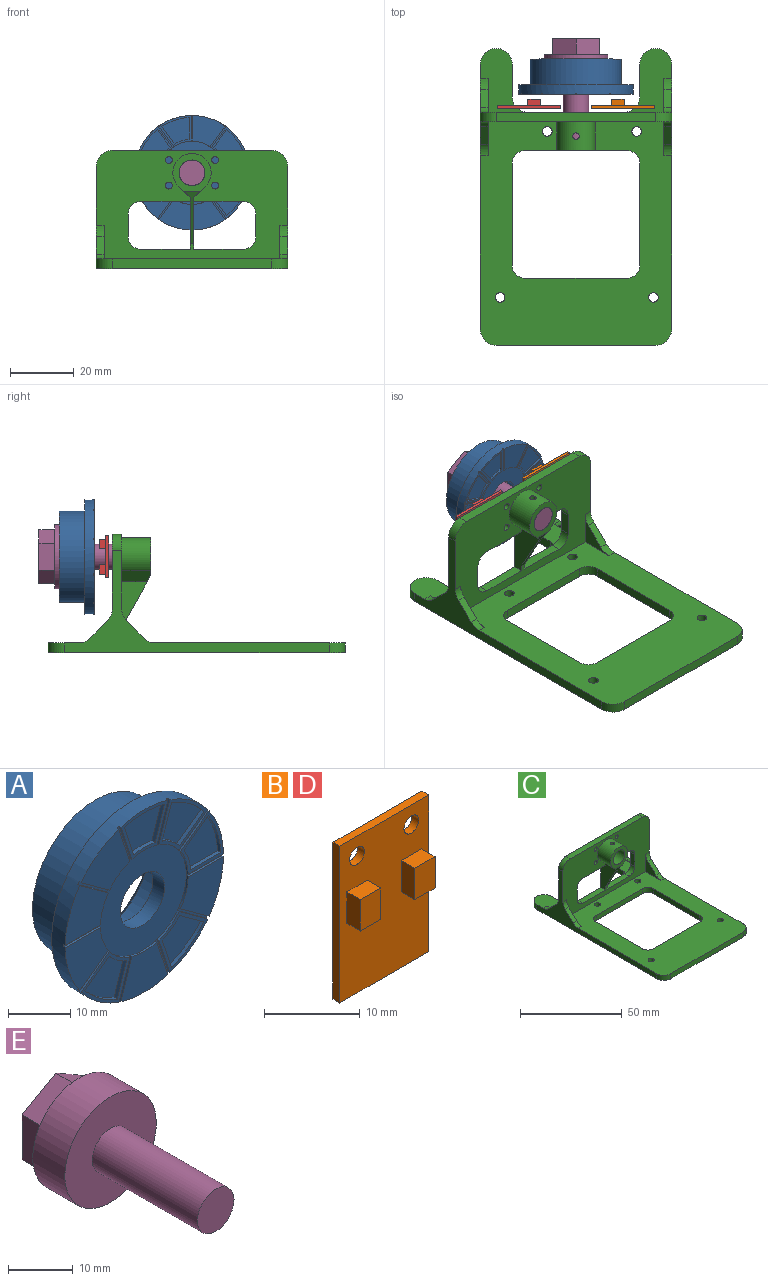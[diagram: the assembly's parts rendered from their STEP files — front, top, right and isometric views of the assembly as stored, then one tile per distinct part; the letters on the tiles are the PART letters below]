
ASSEMBLY  parts=5 mates=4
PART A: 125 faces, bbox 35.9x11.1x35.9 mm
  f0: plane 10.61x8.41mm, normal (0,-1,0), area 18.1mm2, adj f5,f6,f15,f16,f24,f27,f83,f84
  f1: plane 11.06x10.94mm, normal (0,-1,0), area 18.1mm2, adj f5,f6,f25,f26,f29,f32,f78,f79
  f2: plane 10.09x9.75mm, normal (0,-1,0), area 18.1mm2, adj f5,f6,f30,f31,f34,f37,f73,f74
  f3: plane 11.06x10.94mm, normal (0,-1,0), area 18.1mm2, adj f5,f6,f40,f41,f44,f47,f68,f69
  f4: plane 11.06x10.94mm, normal (0,-1,0), area 18.1mm2, adj f5,f6,f50,f51,f54,f57,f63,f64
  f5: cylinder r=17.94mm len=35.89mm, axis (0,1,0), area 345.3mm2, adj f0,f1,f2,f3,f4,f7,f8,f9
  f6: cylinder r=9.94mm len=19.89mm, axis (0,1,0), area 25.5mm2, adj f0,f1,f2,f3,f4,f7,f8,f9
  f7: plane 10.09x9.75mm, normal (0,-1,0), area 66.1mm2, adj f5,f6,f55,f56,f59,f62
  f8: plane 10.09x9.75mm, normal (0,-1,0), area 66.1mm2, adj f5,f6,f19,f22,f60,f61
  f9: plane 10.61x8.41mm, normal (0,-1,0), area 66.1mm2, adj f5,f6,f45,f46,f49,f52
  f10: plane 10.09x9.75mm, normal (0,-1,0), area 66.1mm2, adj f5,f6,f35,f36,f39,f42
  f11: plane 11.06x10.94mm, normal (0,-1,0), area 66.1mm2, adj f5,f6,f14,f17,f20,f21
  f12: plane 19.89x19.89mm, normal (0,-1,0), area 232.1mm2, adj f6,f94
  f13: plane 7.76x2.95mm, normal (0,-1,0), area 4mm2, adj f5,f6,f14,f15,f16,f17
  f14: plane 7.61x2.47mm, normal (0.95,0,0.31), area 3.2mm2, adj f5,f11,f13,f17
  f15: cylinder r=0.25mm len=0.4mm, axis (0,-1,0), area 0mm2, adj f0,f6,f13,f16
  f16: plane 7.61x2.47mm, normal (-0.95,0,-0.31), area 3.2mm2, adj f0,f5,f13,f15
  f17: cylinder r=0.25mm len=0.4mm, axis (0,-1,0), area 0mm2, adj f6,f11,f13,f14
  f18: plane 6.77x5.11mm, normal (0,-1,0), area 4mm2, adj f5,f6,f19,f20,f21,f22
  f19: plane 6.47x4.7mm, normal (0.59,0,0.81), area 3.2mm2, adj f5,f8,f18,f22
  f20: cylinder r=0.25mm len=0.4mm, axis (0,-1,0), area 0mm2, adj f6,f11,f18,f21
  f21: plane 6.47x4.7mm, normal (-0.59,0,-0.81), area 3.2mm2, adj f5,f11,f18,f20
  f22: cylinder r=0.25mm len=0.4mm, axis (0,-1,0), area 0mm2, adj f6,f8,f18,f19
  f23: plane 7.76x2.95mm, normal (0,-1,0), area 4mm2, adj f5,f6,f24,f25,f26,f27
  f24: plane 7.61x2.47mm, normal (0.95,0,-0.31), area 3.2mm2, adj f0,f5,f23,f27
  f25: cylinder r=0.25mm len=0.4mm, axis (0,-1,0), area 0mm2, adj f1,f6,f23,f26
  f26: plane 7.61x2.47mm, normal (-0.95,0,0.31), area 3.2mm2, adj f1,f5,f23,f25
  f27: cylinder r=0.25mm len=0.4mm, axis (0,-1,0), area 0mm2, adj f0,f6,f23,f24
  f28: plane 6.77x5.11mm, normal (0,-1,0), area 4mm2, adj f5,f6,f29,f30,f31,f32
  f29: plane 6.47x4.7mm, normal (0.59,0,-0.81), area 3.2mm2, adj f1,f5,f28,f32
  f30: cylinder r=0.25mm len=0.4mm, axis (0,-1,0), area 0mm2, adj f2,f6,f28,f31
  f31: plane 6.47x4.7mm, normal (-0.59,0,0.81), area 3.2mm2, adj f2,f5,f28,f30
  f32: cylinder r=0.25mm len=0.4mm, axis (0,-1,0), area 0mm2, adj f1,f6,f28,f29
  f33: plane 8x0.5mm, normal (0,-1,0), area 4mm2, adj f5,f6,f34,f35,f36,f37
  f34: plane 8x0.4mm, normal (0,0,-1), area 3.2mm2, adj f2,f5,f33,f37
  f35: cylinder r=0.25mm len=0.4mm, axis (0,-1,0), area 0mm2, adj f6,f10,f33,f36
  f36: plane 8x0.4mm, normal (0,0,1), area 3.2mm2, adj f5,f10,f33,f35
  f37: cylinder r=0.25mm len=0.4mm, axis (0,-1,0), area 0mm2, adj f2,f6,f33,f34
  f38: plane 6.77x5.11mm, normal (0,-1,0), area 4mm2, adj f5,f6,f39,f40,f41,f42
  f39: plane 6.47x4.7mm, normal (-0.59,0,-0.81), area 3.2mm2, adj f5,f10,f38,f42
  f40: cylinder r=0.25mm len=0.4mm, axis (0,-1,0), area 0mm2, adj f3,f6,f38,f41
  f41: plane 6.47x4.7mm, normal (0.59,0,0.81), area 3.2mm2, adj f3,f5,f38,f40
  f42: cylinder r=0.25mm len=0.4mm, axis (0,-1,0), area 0mm2, adj f6,f10,f38,f39
  f43: plane 7.76x2.95mm, normal (0,-1,0), area 4mm2, adj f5,f6,f44,f45,f46,f47
  f44: plane 7.61x2.47mm, normal (-0.95,0,-0.31), area 3.2mm2, adj f3,f5,f43,f47
  f45: cylinder r=0.25mm len=0.4mm, axis (0,-1,0), area 0mm2, adj f6,f9,f43,f46
  f46: plane 7.61x2.47mm, normal (0.95,0,0.31), area 3.2mm2, adj f5,f9,f43,f45
  f47: cylinder r=0.25mm len=0.4mm, axis (0,-1,0), area 0mm2, adj f3,f6,f43,f44
  f48: plane 7.76x2.95mm, normal (0,-1,0), area 4mm2, adj f5,f6,f49,f50,f51,f52
  f49: plane 7.61x2.47mm, normal (-0.95,0,0.31), area 3.2mm2, adj f5,f9,f48,f52
  f50: cylinder r=0.25mm len=0.4mm, axis (0,-1,0), area 0mm2, adj f4,f6,f48,f51
  f51: plane 7.61x2.47mm, normal (0.95,0,-0.31), area 3.2mm2, adj f4,f5,f48,f50
  f52: cylinder r=0.25mm len=0.4mm, axis (0,-1,0), area 0mm2, adj f6,f9,f48,f49
  f53: plane 6.77x5.11mm, normal (0,-1,0), area 4mm2, adj f5,f6,f54,f55,f56,f57
  f54: plane 6.47x4.7mm, normal (-0.59,0,0.81), area 3.2mm2, adj f4,f5,f53,f57
  f55: cylinder r=0.25mm len=0.4mm, axis (0,-1,0), area 0mm2, adj f6,f7,f53,f56
  f56: plane 6.47x4.7mm, normal (0.59,0,-0.81), area 3.2mm2, adj f5,f7,f53,f55
  f57: cylinder r=0.25mm len=0.4mm, axis (0,-1,0), area 0mm2, adj f4,f6,f53,f54
  f58: plane 8x0.5mm, normal (0,-1,0), area 4mm2, adj f5,f6,f59,f60,f61,f62
  f59: plane 8x0.4mm, normal (0,0,1), area 3.2mm2, adj f5,f7,f58,f62
  f60: cylinder r=0.25mm len=0.4mm, axis (0,-1,0), area 0mm2, adj f6,f8,f58,f61
  f61: plane 8x0.4mm, normal (0,0,-1), area 3.2mm2, adj f5,f8,f58,f60
  f62: cylinder r=0.25mm len=0.4mm, axis (0,-1,0), area 0mm2, adj f6,f7,f58,f59
  f63: plane 5.51x4.01mm, normal (0.59,0,-0.81), area 4.9mm2, adj f4,f65,f66,f67
  f64: plane 6.48x2.11mm, normal (-0.95,0,0.31), area 4.9mm2, adj f4,f65,f66,f67
  f65: cylinder r=17.34mm len=7.35mm, axis (0,1,0), area 6.6mm2, adj f4,f63,f64,f67
  f66: cylinder r=10.54mm len=3.95mm, axis (0,1,0), area 3.5mm2, adj f4,f63,f64,f67
  f67: plane 9.46x9.35mm, normal (0,-1,0), area 48mm2, adj f63,f64,f65,f66
  f68: plane 6.48x2.11mm, normal (0.95,0,0.31), area 4.9mm2, adj f3,f70,f71,f72
  f69: plane 5.51x4.01mm, normal (-0.59,0,-0.81), area 4.9mm2, adj f3,f70,f71,f72
  f70: cylinder r=17.34mm len=7.35mm, axis (0,1,0), area 6.6mm2, adj f3,f68,f69,f72
  f71: cylinder r=10.54mm len=3.95mm, axis (0,1,0), area 3.5mm2, adj f3,f68,f69,f72
  f72: plane 9.46x9.35mm, normal (0,-1,0), area 48mm2, adj f68,f69,f70,f71
  f73: plane 6.81x0.72mm, normal (0,0,1), area 4.9mm2, adj f2,f75,f76,f77
  f74: plane 5.51x4.01mm, normal (0.59,0,-0.81), area 4.9mm2, adj f2,f75,f76,f77
  f75: cylinder r=17.34mm len=8.64mm, axis (0,1,0), area 6.6mm2, adj f2,f73,f74,f77
  f76: cylinder r=10.54mm len=4.64mm, axis (0,1,0), area 3.5mm2, adj f2,f73,f74,f77
  f77: plane 8.64x8.32mm, normal (0,-1,0), area 48mm2, adj f73,f74,f75,f76
  f78: plane 5.51x4.01mm, normal (-0.59,0,0.81), area 4.9mm2, adj f1,f80,f81,f82
  f79: plane 6.48x2.11mm, normal (0.95,0,-0.31), area 4.9mm2, adj f1,f80,f81,f82
  f80: cylinder r=17.34mm len=7.35mm, axis (0,1,0), area 6.6mm2, adj f1,f78,f79,f82
  f81: cylinder r=10.54mm len=3.95mm, axis (0,1,0), area 3.5mm2, adj f1,f78,f79,f82
  f82: plane 9.46x9.35mm, normal (0,-1,0), area 48mm2, adj f78,f79,f80,f81
  f83: plane 6.48x2.11mm, normal (-0.95,0,0.31), area 4.9mm2, adj f0,f85,f86,f87
  f84: plane 6.48x2.11mm, normal (0.95,0,0.31), area 4.9mm2, adj f0,f85,f86,f87
  f85: cylinder r=17.34mm len=9.09mm, axis (0,1,0), area 6.6mm2, adj f0,f83,f84,f87
  f86: cylinder r=10.54mm len=4.88mm, axis (0,1,0), area 3.5mm2, adj f0,f83,f84,f87
  f87: plane 9.09x7.09mm, normal (0,-1,0), area 48mm2, adj f83,f84,f85,f86
  f88: plane 35.89x35.89mm, normal (0,1,0), area 369.2mm2, adj f5,f90
  f89: cylinder r=11.3mm len=22.6mm, axis (0,-1,0), area 497mm2, adj f92,f93
  f90: cylinder r=14.3mm len=28.6mm, axis (0,-1,0), area 718.8mm2, adj f88,f91
  f91: plane 28.6x28.6mm, normal (0,1,0), area 167.1mm2, adj f90,f93
  f92: plane 22.6x22.6mm, normal (0,1,0), area 322.6mm2, adj f89,f94
  f93: cone r=11.3mm half-angle=45deg, axis (0,1,0), area 104.9mm2, adj f89,f91
  f94: cylinder r=5mm len=10mm, axis (0,1,0), area 82.9mm2, adj f12,f92
  f95: cylinder r=10.54mm len=4.88mm, axis (0,1,0), area 0.6mm2, adj f97,f98,f99,f100
  f96: cylinder r=17.34mm len=9.09mm, axis (0,1,0), area 1.1mm2, adj f97,f98,f99,f100
  f97: plane 9.09x7.09mm, normal (0,1,0), area 48mm2, adj f95,f96,f99,f100
  f98: plane 9.09x7.09mm, normal (0,-1,0), area 48mm2, adj f95,f96,f99,f100
  f99: plane 6.48x2.11mm, normal (-0.95,0,-0.31), area 0.8mm2, adj f95,f96,f97,f98
  f100: plane 6.48x2.11mm, normal (0.95,0,-0.31), area 0.8mm2, adj f95,f96,f97,f98
  f101: plane 5.51x4.01mm, normal (0.59,0,0.81), area 0.8mm2, adj f103,f104,f105,f106
  f102: plane 6.81x0.12mm, normal (0,0,-1), area 0.8mm2, adj f103,f104,f105,f106
  f103: plane 8.64x8.32mm, normal (0,1,0), area 48mm2, adj f101,f102,f104,f105
  f104: cylinder r=17.34mm len=8.64mm, axis (0,1,0), area 1.1mm2, adj f101,f102,f103,f106
  f105: cylinder r=10.54mm len=4.64mm, axis (0,1,0), area 0.6mm2, adj f101,f102,f103,f106
  f106: plane 8.64x8.32mm, normal (0,-1,0), area 48mm2, adj f101,f102,f104,f105
  f107: plane 5.51x4.01mm, normal (0.59,0,0.81), area 0.8mm2, adj f109,f110,f111,f112
  f108: plane 6.48x2.11mm, normal (-0.95,0,-0.31), area 0.8mm2, adj f109,f110,f111,f112
  f109: plane 9.46x9.35mm, normal (0,1,0), area 48mm2, adj f107,f108,f110,f111
  f110: cylinder r=17.34mm len=7.35mm, axis (0,1,0), area 1.1mm2, adj f107,f108,f109,f112
  f111: cylinder r=10.54mm len=3.95mm, axis (0,1,0), area 0.6mm2, adj f107,f108,f109,f112
  f112: plane 9.46x9.35mm, normal (0,-1,0), area 48mm2, adj f107,f108,f110,f111
  f113: plane 6.81x0.12mm, normal (0,0,1), area 0.8mm2, adj f115,f116,f117,f118
  f114: plane 5.51x4.01mm, normal (-0.59,0,-0.81), area 0.8mm2, adj f115,f116,f117,f118
  f115: plane 8.64x8.32mm, normal (0,1,0), area 48mm2, adj f113,f114,f116,f117
  f116: cylinder r=17.34mm len=8.64mm, axis (0,1,0), area 1.1mm2, adj f113,f114,f115,f118
  f117: cylinder r=10.54mm len=4.64mm, axis (0,1,0), area 0.6mm2, adj f113,f114,f115,f118
  f118: plane 8.64x8.32mm, normal (0,-1,0), area 48mm2, adj f113,f114,f116,f117
  f119: plane 6.81x0.12mm, normal (0,0,-1), area 0.8mm2, adj f121,f122,f123,f124
  f120: plane 5.51x4.01mm, normal (-0.59,0,0.81), area 0.8mm2, adj f121,f122,f123,f124
  f121: plane 8.64x8.32mm, normal (0,1,0), area 48mm2, adj f119,f120,f122,f123
  f122: cylinder r=17.34mm len=8.64mm, axis (0,1,0), area 1.1mm2, adj f119,f120,f121,f124
  f123: cylinder r=10.54mm len=4.64mm, axis (0,1,0), area 0.6mm2, adj f119,f120,f121,f124
  f124: plane 8.64x8.32mm, normal (0,-1,0), area 48mm2, adj f119,f120,f122,f123
PART B: 18 faces, bbox 13.1x3x20 mm
  f0: plane 13.1x1mm, normal (0,0,1), area 13.1mm2, adj f1,f5,f6,f7
  f1: plane 20x1mm, normal (-1,0,0), area 20mm2, adj f0,f2,f6,f7
  f2: plane 13.1x1mm, normal (0,0,-1), area 13.1mm2, adj f1,f5,f6,f7
  f3: cylinder r=1.09mm len=2.18mm, axis (0,1,0), area 6.8mm2, adj f6,f7
  f4: cylinder r=1.09mm len=2.18mm, axis (0,1,0), area 6.8mm2, adj f6,f7
  f5: plane 20x1mm, normal (1,0,0), area 20mm2, adj f0,f2,f6,f7
  f6: plane 20x13.1mm, normal (0,-1,0), area 230.5mm2, adj f0,f1,f2,f3,f4,f5,f9,f10
  f7: plane 20x13.1mm, normal (0,1,0), area 254.5mm2, adj f0,f1,f2,f3,f4,f5
  f8: plane 4x3mm, normal (0,-1,0), area 12mm2, adj f9,f10,f11,f12
  f9: plane 4x2mm, normal (-1,0,0), area 8mm2, adj f6,f8,f10,f12
  f10: plane 3x2mm, normal (0,0,1), area 6mm2, adj f6,f8,f9,f11
  f11: plane 4x2mm, normal (1,0,0), area 8mm2, adj f6,f8,f10,f12
  f12: plane 3x2mm, normal (0,0,-1), area 6mm2, adj f6,f8,f9,f11
  f13: plane 4x3mm, normal (0,-1,0), area 12mm2, adj f14,f15,f16,f17
  f14: plane 3x2mm, normal (0,0,1), area 6mm2, adj f6,f13,f15,f17
  f15: plane 4x2mm, normal (1,0,0), area 8mm2, adj f6,f13,f14,f16
  f16: plane 3x2mm, normal (0,0,-1), area 6mm2, adj f6,f13,f15,f17
  f17: plane 4x2mm, normal (-1,0,0), area 8mm2, adj f6,f13,f14,f16
PART C: 71 faces, bbox 60x93x37 mm
  f0: cylinder r=6mm len=12mm, axis (0,1,0), area 251.3mm2, adj f7,f17,f65,f66,f67
  f1: plane 15.4x3mm, normal (0,0,-1), area 46.2mm2, adj f5,f7,f34,f68
  f2: plane 15.4x3mm, normal (0,0,1), area 46.2mm2, adj f5,f7,f36,f68
  f3: cylinder r=4mm len=12mm, axis (0,1,0), area 298.4mm2, adj f5,f17,f65
  f4: plane 20x15mm, normal (0,0,1), area 168.2mm2, adj f5,f11,f39,f47,f50,f57,f58
  f5: plane 60x37mm, normal (0,1,0), area 1433mm2, adj f1,f2,f3,f4,f6,f8,f10,f11
  f6: plane 20x15mm, normal (0,0,1), area 168.2mm2, adj f5,f16,f40,f44,f54,f59,f60
  f7: plane 60x34mm, normal (0,-1,0), area 1255.7mm2, adj f0,f1,f2,f9,f10,f11,f12,f13
  f8: plane 93x60mm, normal (0,0,-1), area 3144mm2, adj f5,f11,f16,f18,f19,f20,f21,f22
  f9: plane 70x60mm, normal (0,0,1), area 2521.9mm2, adj f7,f11,f16,f18,f19,f20,f21,f22
  f10: plane 50x3mm, normal (0,0,1), area 150mm2, adj f5,f7,f63,f64
  f11: plane 83x32mm, normal (-1,0,0), area 410.2mm2, adj f4,f5,f7,f8,f9,f46,f48,f49
  f12: cylinder r=1.09mm len=3mm, axis (0,1,0), area 20.5mm2, adj f5,f7
  f13: cylinder r=1.09mm len=3mm, axis (0,1,0), area 20.5mm2, adj f5,f7
  f14: cylinder r=1.09mm len=3mm, axis (0,1,0), area 20.5mm2, adj f5,f7
  f15: cylinder r=1.09mm len=3mm, axis (0,1,0), area 20.5mm2, adj f5,f7
  f16: plane 83x32mm, normal (1,0,0), area 410.2mm2, adj f5,f6,f7,f8,f9,f41,f43,f53
  f17: plane 12x12mm, normal (0,-1,0), area 64.4mm2, adj f0,f3,f66,f67,f70
  f18: plane 50x3mm, normal (0,-1,0), area 150mm2, adj f8,f9,f61,f62
  f19: cylinder r=1.5mm len=3mm, axis (0,0,1), area 28.3mm2, adj f8,f9
  f20: cylinder r=1.5mm len=3mm, axis (0,0,1), area 28.3mm2, adj f8,f9
  f21: cylinder r=1.5mm len=3mm, axis (0,0,1), area 28.3mm2, adj f8,f9
  f22: cylinder r=1.5mm len=3mm, axis (0,0,1), area 28.3mm2, adj f8,f9
  f23: plane 32x3mm, normal (-1,0,0), area 96mm2, adj f8,f9,f24,f30
  f24: cylinder r=4mm len=4mm, axis (0,0,1), area 18.8mm2, adj f8,f9,f23,f25
  f25: plane 32x3mm, normal (0,-1,0), area 96mm2, adj f8,f9,f24,f26
  f26: cylinder r=4mm len=4mm, axis (0,0,1), area 18.8mm2, adj f8,f9,f25,f27
  f27: plane 32x3mm, normal (1,0,0), area 96mm2, adj f8,f9,f26,f28
  f28: cylinder r=4mm len=4mm, axis (0,0,1), area 18.8mm2, adj f8,f9,f27,f29
  f29: plane 32x3mm, normal (0,1,0), area 96mm2, adj f8,f9,f28,f30
  f30: cylinder r=4mm len=4mm, axis (0,0,1), area 18.8mm2, adj f8,f9,f23,f29
  f31: plane 7x3mm, normal (-1,0,0), area 21mm2, adj f5,f7,f32,f38
  f32: cylinder r=4mm len=4mm, axis (0,-1,0), area 18.8mm2, adj f5,f7,f31,f33
  f33: plane 15.4x3mm, normal (0,0,-1), area 46.2mm2, adj f5,f7,f32,f69
  f34: cylinder r=4mm len=4mm, axis (0,-1,0), area 18.8mm2, adj f1,f5,f7,f35
  f35: plane 7x3mm, normal (1,0,0), area 21mm2, adj f5,f7,f34,f36
  f36: cylinder r=4mm len=4mm, axis (0,-1,0), area 18.8mm2, adj f2,f5,f7,f35
  f37: plane 15.4x3mm, normal (0,0,1), area 46.2mm2, adj f5,f7,f38,f69
  f38: cylinder r=4mm len=4mm, axis (0,-1,0), area 18.8mm2, adj f5,f7,f31,f37
  f39: plane 10x3mm, normal (1,0,0), area 30mm2, adj f4,f8,f57,f58
  f40: plane 10x3mm, normal (-1,0,0), area 30mm2, adj f6,f8,f59,f60
  f41: plane 5.56x5.56mm, normal (0,-0.71,0.71), area 19.6mm2, adj f16,f42,f55,f56
  f42: plane 10.56x10.56mm, normal (-1,0,0), area 37.1mm2, adj f7,f9,f41,f55,f56
  f43: plane 5.56x5.56mm, normal (0,0.71,0.71), area 19.6mm2, adj f16,f44,f53,f54
  f44: plane 10.56x10.56mm, normal (-1,0,0), area 37.1mm2, adj f5,f6,f43,f53,f54
  f45: plane 10.56x10.56mm, normal (1,0,0), area 37.1mm2, adj f7,f9,f46,f51,f52
  f46: plane 5.56x5.56mm, normal (0,-0.71,0.71), area 19.6mm2, adj f11,f45,f51,f52
  f47: plane 10.56x10.56mm, normal (1,0,0), area 37.1mm2, adj f4,f5,f48,f49,f50
  f48: plane 5.56x5.56mm, normal (0,0.71,0.71), area 19.6mm2, adj f11,f47,f49,f50
  f49: cylinder r=5mm len=3.54mm, axis (-1,0,0), area 9.8mm2, adj f5,f11,f47,f48
  f50: cylinder r=5mm len=3.54mm, axis (1,0,0), area 9.8mm2, adj f4,f11,f47,f48
  f51: cylinder r=5mm len=3.54mm, axis (-1,0,0), area 9.8mm2, adj f7,f11,f45,f46
  f52: cylinder r=5mm len=3.54mm, axis (-1,0,0), area 9.8mm2, adj f9,f11,f45,f46
  f53: cylinder r=5mm len=3.54mm, axis (-1,0,0), area 9.8mm2, adj f5,f16,f43,f44
  f54: cylinder r=5mm len=3.54mm, axis (1,0,0), area 9.8mm2, adj f6,f16,f43,f44
  f55: cylinder r=5mm len=3.54mm, axis (-1,0,0), area 9.8mm2, adj f9,f16,f41,f42
  f56: cylinder r=5mm len=3.54mm, axis (-1,0,0), area 9.8mm2, adj f7,f16,f41,f42
  f57: cylinder r=5mm len=10mm, axis (0,0,1), area 47.1mm2, adj f4,f8,f11,f39
  f58: cylinder r=5mm len=5mm, axis (0,0,1), area 23.6mm2, adj f4,f5,f8,f39
  f59: cylinder r=5mm len=5mm, axis (0,0,-1), area 23.6mm2, adj f5,f6,f8,f40
  f60: cylinder r=5mm len=10mm, axis (0,0,1), area 47.1mm2, adj f6,f8,f16,f40
  f61: cylinder r=5mm len=5mm, axis (0,0,-1), area 23.6mm2, adj f8,f9,f11,f18
  f62: cylinder r=5mm len=5mm, axis (0,0,-1), area 23.6mm2, adj f8,f9,f16,f18
  f63: cylinder r=5mm len=5mm, axis (0,-1,0), area 23.6mm2, adj f5,f7,f10,f11
  f64: cylinder r=5mm len=5mm, axis (0,1,0), area 23.6mm2, adj f5,f7,f10,f16
  f65: cylinder r=1mm len=2.13mm, axis (0,0,1), area 12.7mm2, adj f0,f3
  f66: plane 9x3.64mm, normal (-0.71,0,-0.71), area 45mm2, adj f0,f7,f17,f68,f70
  f67: plane 9x3.64mm, normal (0.71,0,-0.71), area 45mm2, adj f0,f7,f17,f69,f70
  f68: plane 16.11x10.95mm, normal (-1,0,0), area 101.9mm2, adj f1,f2,f5,f7,f66,f70
  f69: plane 16.11x10.95mm, normal (1,0,0), area 101.9mm2, adj f5,f7,f33,f37,f67,f70
  f70: plane 16.2x9mm, normal (0,-0.87,-0.49), area 26.3mm2, adj f7,f17,f66,f67,f68,f69
PART D: same geometry as B
PART E: 12 faces, bbox 20x35x20 mm
  f0: plane 8.5x5mm, normal (1,0,0), area 42.5mm2, adj f1,f5,f6,f7
  f1: plane 7.36x5mm, normal (0.5,0,0.87), area 42.5mm2, adj f0,f2,f6,f7
  f2: plane 7.36x5mm, normal (-0.5,0,0.87), area 42.5mm2, adj f1,f3,f6,f7
  f3: plane 8.5x5mm, normal (-1,0,0), area 42.5mm2, adj f2,f4,f6,f7
  f4: plane 7.36x5mm, normal (-0.5,0,-0.87), area 42.5mm2, adj f3,f5,f6,f7
  f5: plane 7.36x5mm, normal (0.5,0,-0.87), area 42.5mm2, adj f0,f4,f6,f7
  f6: plane 17x14.72mm, normal (0,1,0), area 187.7mm2, adj f0,f1,f2,f3,f4,f5
  f7: plane 20x20mm, normal (0,1,0), area 126.4mm2, adj f0,f1,f2,f3,f4,f5,f8
  f8: cylinder r=10mm len=20mm, axis (0,1,0), area 439.8mm2, adj f7,f9
  f9: plane 20x20mm, normal (0,-1,0), area 263.9mm2, adj f8,f11
  f10: plane 8x8mm, normal (0,-1,0), area 50.3mm2, adj f11
  f11: cylinder r=4mm len=23mm, axis (0,1,0), area 578.1mm2, adj f9,f10
PLACE A rot(axis=(0,-1,0),90deg) t=(0,6.88,0)mm
PLACE B rot(axis=(0.71,0,-0.71),180deg) t=(13.1,1.1,0)mm
PLACE C at identity fixed
PLACE D rot(axis=(-0.71,0,-0.71),180deg) t=(-13.1,1.1,0)mm
PLACE E t=(0,23,0)mm
MATE fastened C.f12 <-> D.f3  axis (0,-1,0) through (-7.25,0,4)mm
MATE fastened C.f14 <-> B.f3  axis (0,-1,0) through (7.25,0,-4)mm
MATE revolute C.f3 <-> A.f5  axis (0,1,0) through (0,0,0)mm
MATE fastened C.f3 <-> E.f11  axis (0,1,0) through (0,0,0)mm
